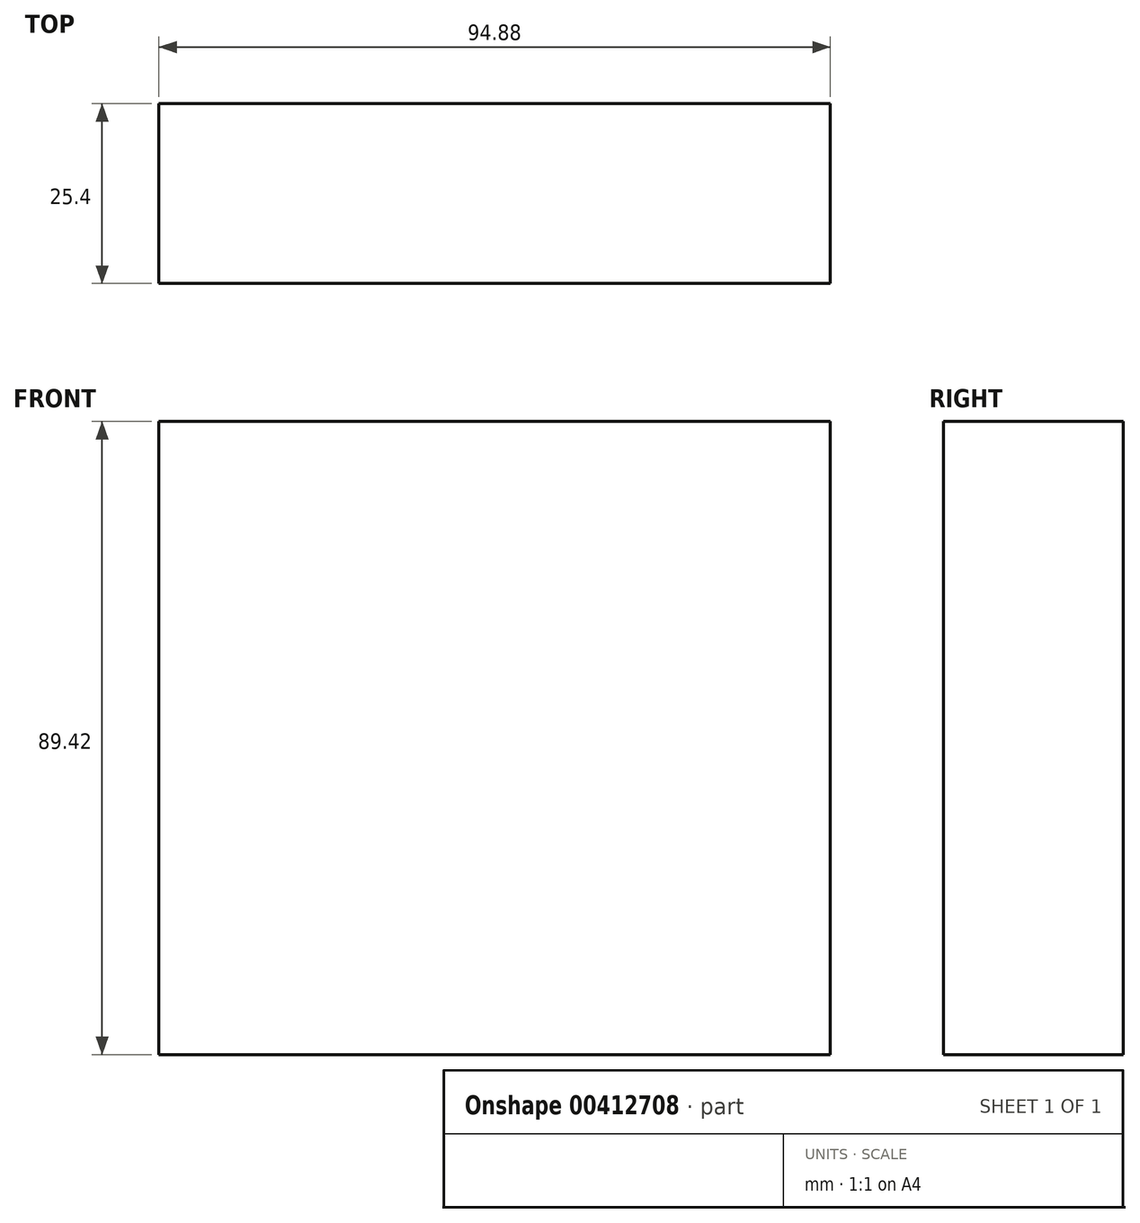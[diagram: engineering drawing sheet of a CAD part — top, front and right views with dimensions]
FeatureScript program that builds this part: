
annotation { "Feature Type Name" : "Feature", "Feature Type Description" : "" }
export const myFeature = defineFeature(function(context is Context, id is Id, definition is map)
    precondition{}
    {
        {
            var Q0;
            Q0=qCreatedBy(makeId("Front.planeOp"),FACE);
            var sketch = newSketch(context, id + "F0", { "sketchPlane" : qUnion([Q0])});
            skLineSegment(sketch, "E0.bottom", {"start": v(-39.15, 41.41) * mm, "end": v(55.73, 41.41) * mm});
            skLineSegment(sketch, "E0.top", {"start": v(-39.15, -48.01) * mm, "end": v(55.73, -48.01) * mm});
            skLineSegment(sketch, "E0.left", {"start": v(-39.15, 41.41) * mm, "end": v(-39.15, -48.01) * mm});
            skLineSegment(sketch, "E0.right", {"start": v(55.73, 41.41) * mm, "end": v(55.73, -48.01) * mm});
            skSolve(sketch);
        }
        {
            var Q0;
            Q0=makeQuery(id+"F0.imprint","IMPRINT",FACE,{"disambiguationData":[TD([[makeQuery(id+"F0.imprint","IMPRINT",EDGE,{"derivedFrom":sQuery(id+"F0.wireOp",EDGE,"E0.bottom")}),-1.0]])]});
            extrude(context, id + "F1", {"entities" : qUnion([Q0]), "depth" : 25.4 * mm});
        }
    });
